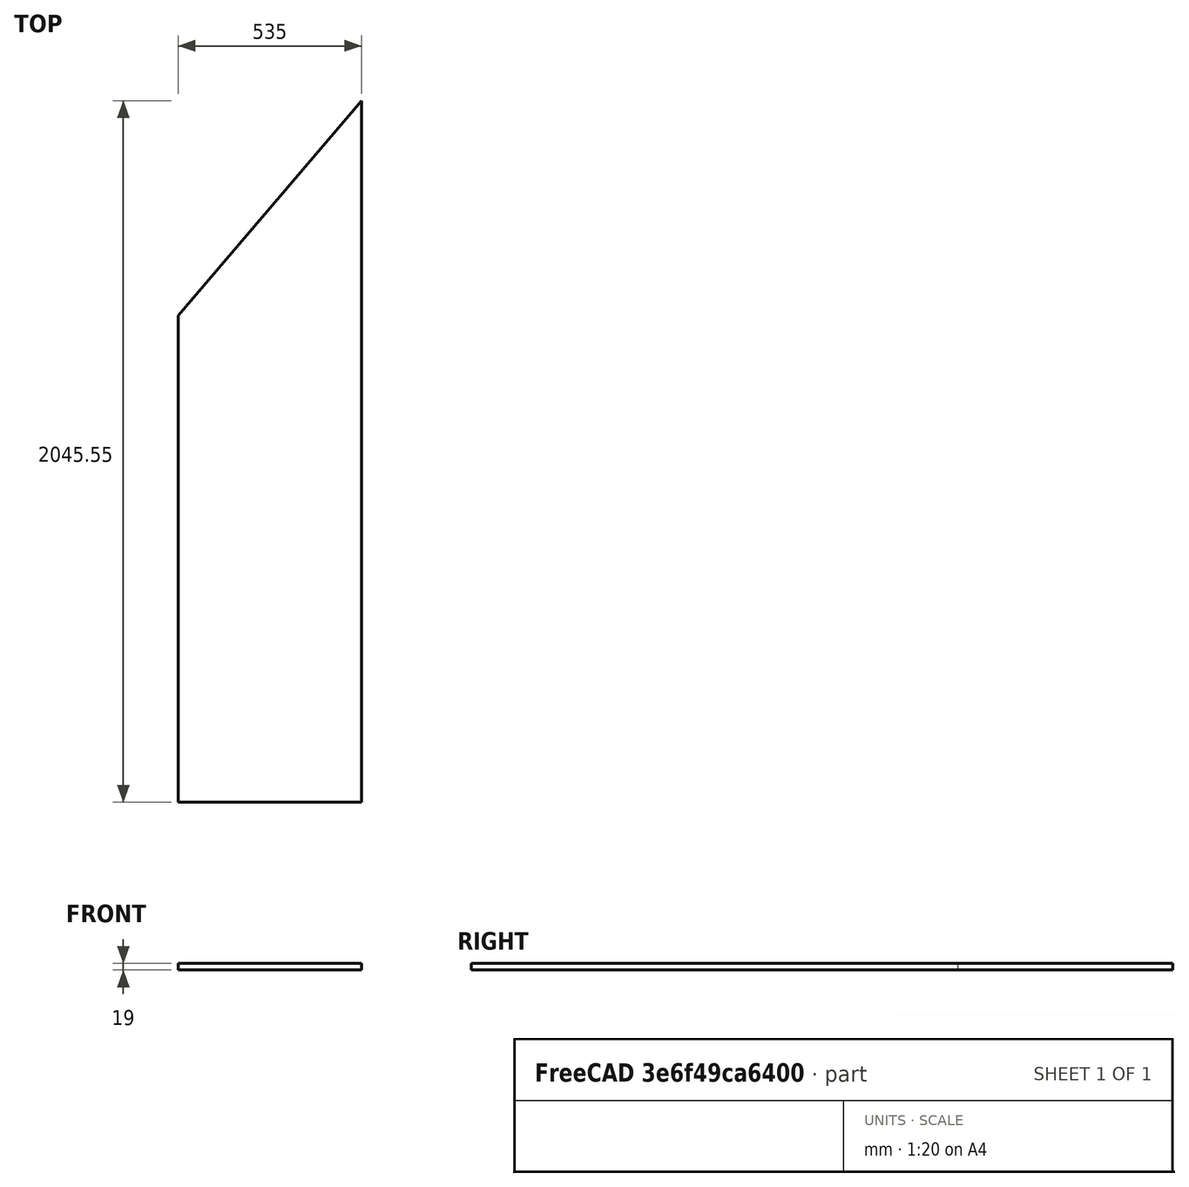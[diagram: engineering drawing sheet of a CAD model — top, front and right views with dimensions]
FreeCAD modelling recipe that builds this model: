
FCSTD DOCUMENT  (FreeCAD 1.0R39285 (Git))
Label: wardrobe_door_corpus01_jan
License: All rights reserved
LicenseURL: https://en.wikipedia.org/wiki/All_rights_reserved
objects: TechDraw::DrawViewDimension×6, PartDesign::CoordinateSystem×2, TechDraw::DrawProjGroupItem×2, Sketcher::SketchObject×1, PartDesign::Pad×1, PartDesign::Body×1, TechDraw::DrawSVGTemplate×1, TechDraw::DrawViewAnnotation×1, App::Part×1, TechDraw::DrawPage×1
note: 16 computed .brp shape members not serialized (recipe doc carries the construction recipe); baked Part::Feature solids carry a one-line shape summary decoded from their .brp
EXTERNAL_REF file=../../mastersheet.FCStd obj=Spreadsheet
EXTERNAL_REF file=../../mastersketch.FCStd obj=Sketch

FEATURE [Sketcher::SketchObject] Sketch
  ArcFitTolerance = 1e-06
  AttachmentSupport = -> [XY_Plane]
  FullyConstrained = true
  MakeInternals = false
  MapMode = 5
  expr: Constraints[0] = mastersketch#Sketch.Constraints.corpus01_door_height
  expr: Constraints[10] = mastersketch#Sketch.Constraints.alpha
  expr: Constraints[3] = mastersheet#Spreadsheet.corpus_width - 5
  sketch-geometry (4):
    g0: LineSegment StartX=0 StartY=0 StartZ=0 EndX=0 EndY=2045.55 EndZ=0
    g1: LineSegment StartX=0 StartY=0 StartZ=0 EndX=-535 EndY=0 EndZ=0
    g2: LineSegment StartX=-535 StartY=0 StartZ=0 EndX=-535 EndY=1419.54 EndZ=0
    g3: LineSegment StartX=-535 StartY=1419.54 StartZ=0 EndX=0 EndY=2045.55 EndZ=0
  constraints (11):
    c: Distance(g0) = 2045.55
    c: Coincident(g0,g-1)
    c: Vertical(g0)
    c: Distance(g1) = 535
    c: Coincident(g1,g0)
    c: PointOnObject(g1,g-1)
    c: Vertical(g2)
    c: Coincident(g3,g2)
    c: Coincident(g2,g1)
    c: Coincident(g3,g0)
    c: Angle(g2,g3) = 2.43442
FEATURE [PartDesign::Pad] Pad
  Direction = (0,0,1)
  Length = 19
  Length2 = 10
  Profile = -> Sketch
  ReferenceAxis = -> Sketch [N_Axis]
  Refine = true
  Suppressed = false
  Type = 0
FEATURE [PartDesign::Body] Body  label="wardrobe_door_corpus01_jan"
  AllowCompound = false
  Group = -> [Sketch,Pad]
  Origin = -> Origin
  Tip = -> Pad
FEATURE [PartDesign::CoordinateSystem] LCS_bottom
  AttacherType = Attacher::AttachEngine3D
  AttachmentSupport = -> [Pad]
  MapMode = 7
  Placement = pos=(0,0,0) rot=(1,0,0;1.5708rad)
FEATURE [TechDraw::DrawSVGTemplate] Template  label="Vorlage"
  Height = 210
  Orientation = 1
  Template = <userpath>/scoop/apps/freecad/current/data/Mod/TechDraw/Templates/A4_Landscape_TD.svg
  Width = 297
FEATURE [TechDraw::DrawProjGroupItem] View
  CoarseView = false
  Direction = (0,0,-1)
  Focus = 100
  HardHidden = false
  IsoCount = 0
  IsoHidden = false
  IsoVisible = false
  LockPosition = false
  Perspective = false
  Rotation = 0
  RotationVector = (1,0,0)
  Scale = 0.1
  ScaleType = 2
  ScrubCount = 1
  SeamHidden = false
  SeamVisible = false
  SmoothHidden = false
  SmoothVisible = true
  Source = -> [Body]
  Type = 0
  X = 141.812
  XDirection = (1e-16,-1,0)
  Y = 151.017
FEATURE [TechDraw::DrawProjGroupItem] View001
  CoarseView = false
  Direction = (-1,-1e-16,-2e-16)
  Focus = 100
  HardHidden = false
  IsoCount = 0
  IsoHidden = false
  IsoVisible = false
  LockPosition = false
  Perspective = false
  Rotation = 0
  RotationVector = (1,0,0)
  Scale = 0.1
  ScaleType = 2
  ScrubCount = 1
  SeamHidden = false
  SeamVisible = false
  SmoothHidden = false
  SmoothVisible = true
  Source = -> [Body]
  Type = 0
  X = 141.812
  XDirection = (1e-16,-1,0)
  Y = 91.1832
FEATURE [TechDraw::DrawViewDimension] Dimension  label="Maß"
  AngleOverride = false
  Arbitrary = false
  ArbitraryTolerances = false
  BoxCorners = (2) [(-102.277,-26.75,0),(102.277,26.75,0)]
  EqualTolerance = true
  ExtensionAngle = 0
  FormatSpec = %.1w
  FormatSpecOverTolerance = %+.2w
  FormatSpecUnderTolerance = %+.2w
  Inverted = false
  LineAngle = 0
  LockPosition = false
  MeasureType = 1
  OverTolerance = 0
  References2D = -> [View]
  Rotation = 0
  ScaleType = 0
  TheoreticalExact = false
  Type = 1
  UnderTolerance = 0
  X = 0
  Y = -31.9684
FEATURE [TechDraw::DrawViewDimension] Dimension001  label="Maß001"
  AngleOverride = false
  Arbitrary = false
  ArbitraryTolerances = false
  BoxCorners = (2) [(-102.277,-26.75,0),(102.277,26.75,0)]
  EqualTolerance = true
  ExtensionAngle = 0
  FormatSpec = %.2w
  FormatSpecOverTolerance = %+.2w
  FormatSpecUnderTolerance = %+.2w
  Inverted = false
  LineAngle = 0
  LockPosition = false
  MeasureType = 1
  OverTolerance = 0
  References2D = -> [View]
  Rotation = 0
  ScaleType = 0
  TheoreticalExact = false
  Type = 2
  UnderTolerance = 0
  X = 110.367
  Y = 0
FEATURE [TechDraw::DrawViewDimension] Dimension002  label="Maß002"
  AngleOverride = false
  Arbitrary = false
  ArbitraryTolerances = false
  BoxCorners = (2) [(-102.277,-0.9,0),(102.277,0.9,0)]
  EqualTolerance = true
  ExtensionAngle = 0
  FormatSpec = %.2w
  FormatSpecOverTolerance = %+.2w
  FormatSpecUnderTolerance = %+.2w
  Inverted = false
  LineAngle = 0
  LockPosition = false
  MeasureType = 1
  OverTolerance = 0
  References2D = -> [View001]
  Rotation = 0
  ScaleType = 0
  TheoreticalExact = false
  Type = 0
  UnderTolerance = 0
  X = 112.07
  Y = -9.57936
FEATURE [TechDraw::DrawViewDimension] Dimension003  label="Maß003"
  AngleOverride = false
  Arbitrary = false
  ArbitraryTolerances = false
  BoxCorners = (2) [(-102.277,-26.75,0),(102.277,26.75,0)]
  EqualTolerance = true
  ExtensionAngle = 0
  FormatSpec = %.1w
  FormatSpecOverTolerance = %+.2w
  FormatSpecUnderTolerance = %+.2w
  Inverted = false
  LineAngle = 0
  LockPosition = false
  MeasureType = 1
  OverTolerance = 0
  References2D = -> [View]
  Rotation = 0
  ScaleType = 0
  TheoreticalExact = false
  Type = 1
  UnderTolerance = 0
  X = 31.3003
  Y = 43.1902
FEATURE [TechDraw::DrawViewDimension] Dimension004  label="Maß004"
  AngleOverride = false
  Arbitrary = false
  ArbitraryTolerances = false
  BoxCorners = (2) [(-102.277,-26.75,0),(102.277,26.75,0)]
  EqualTolerance = true
  ExtensionAngle = 0
  FormatSpec = (%.1w)
  FormatSpecOverTolerance = %+.1w
  FormatSpecUnderTolerance = %+.1w
  Inverted = false
  LineAngle = 0
  LockPosition = false
  MeasureType = 1
  OverTolerance = 0
  References2D = -> [View]
  Rotation = 0
  ScaleType = 0
  TheoreticalExact = false
  Type = 6
  UnderTolerance = 0
  X = -27.5114
  Y = 6.08199
FEATURE [TechDraw::DrawViewAnnotation] Annotation  label="Beschriftung"
  Font = MS Shell Dlg 2
  LineSpace = 100
  LockPosition = false
  MaxWidth = -1
  Rotation = 0
  ScaleType = 0
  Text = Artikelnummer: 12391882 oder 6754673
  TextSize = 5
  TextStyle = 0
  X = 208.306
  Y = 62.1004
FEATURE [PartDesign::CoordinateSystem] LCS_Origin
  AttacherType = Attacher::AttachEngine3D
  AttachmentSupport = -> [X_Axis001]
  MapMode = 2
FEATURE [App::Part] wardrobe_door_corpus01_jan  label="wardrobe_door_corpus01_jan001"
  DrawingName = wardrobe_door_corpus01_jan.FCStd
  Group = -> [LCS_Origin,LCS_bottom,Body]
  Origin = -> Origin001
  PartDescription = wardrobe_door_corpus01_jan
  PartID = wardrobe_door_corpus01_jan
FEATURE [TechDraw::DrawViewDimension] Dimension005  label="Maß005"
  AngleOverride = false
  Arbitrary = false
  ArbitraryTolerances = false
  BoxCorners = (2) [(-102.277,-26.75,0),(102.277,26.75,0)]
  EqualTolerance = true
  ExtensionAngle = 0
  FormatSpec = (%.1w)
  FormatSpecOverTolerance = %+.1w
  FormatSpecUnderTolerance = %+.1w
  Inverted = false
  LineAngle = 0
  LockPosition = false
  MeasureType = 1
  OverTolerance = 0
  References2D = -> [View]
  Rotation = 0
  ScaleType = 0
  TheoreticalExact = false
  Type = 0
  UnderTolerance = 0
  X = -75.6861
  Y = 12.9628
FEATURE [TechDraw::DrawPage] Page  label="Seite"
  KeepUpdated = true
  NextBalloonIndex = 1
  ProjectionType = 0
  Template = -> Template
  Views = -> [View,View001,Dimension,Dimension001,Dimension002,Dimension003,Dimension004,Annotation,Dimension005]
